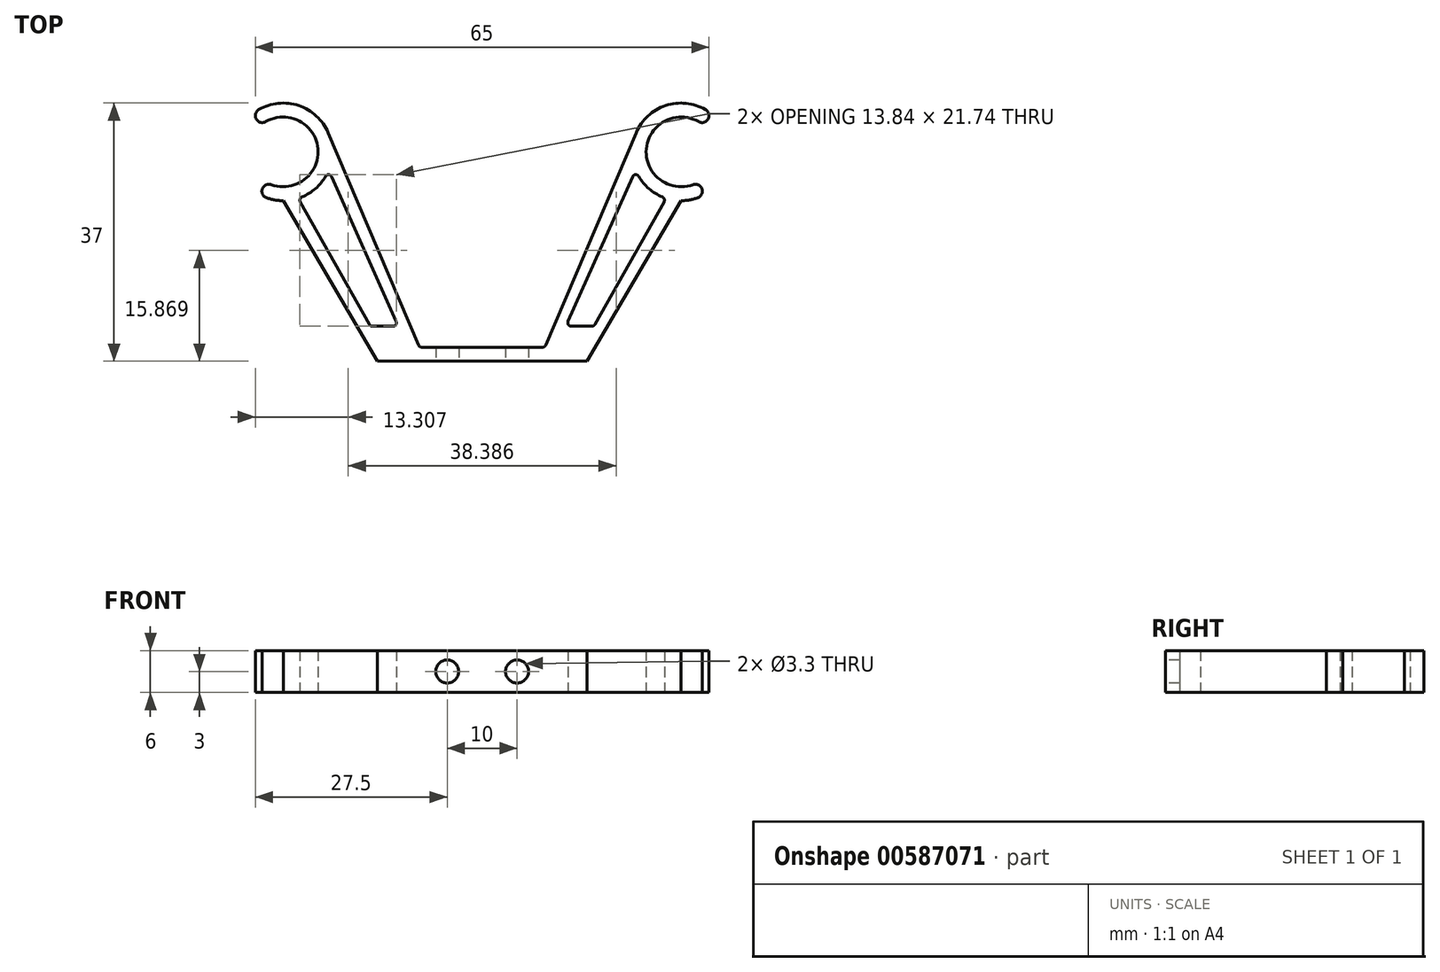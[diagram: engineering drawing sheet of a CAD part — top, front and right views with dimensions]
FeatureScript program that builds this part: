
annotation { "Feature Type Name" : "Feature", "Feature Type Description" : "" }
export const myFeature = defineFeature(function(context is Context, id is Id, definition is map)
    precondition{}
    {
        {
            var Q0;
            Q0=qCreatedBy(makeId("Top.planeOp"),FACE);
            var sketch = newSketch(context, id + "F0", { "sketchPlane" : qUnion([Q0])});
            skLineSegment(sketch, "E0", {"start": v(-28.5, 0) * mm, "end": v(28.5, 0) * mm, "construction": true});
            skArc(sketch, "E1", {"start": v(-31, 4.33) * mm, "mid": v(-23.52, 0.44) * mm, "end": v(-30.21, -4.7) * mm});
            skLineSegment(sketch, "E2", {"start": v(0, 15.66) * mm, "end": v(0, -18.65) * mm, "construction": true});
            skLineSegment(sketch, "E3", {"start": v(-31, 4.33) * mm, "end": v(-28.5, 0) * mm, "construction": true});
            skLineSegment(sketch, "E4", {"start": v(-30.21, -4.7) * mm, "end": v(-28.5, 0) * mm, "construction": true});
            skLineSegment(sketch, "E5", {"start": v(-15, -30) * mm, "end": v(0, -30) * mm});
            skArc(sketch, "E6.0", {"start": v(-32, 6.06) * mm, "mid": v(-26.28, 6.64) * mm, "end": v(-22.06, 2.74) * mm});
            skArc(sketch, "E7", {"start": v(-32, 6.06) * mm, "mid": v(-32.37, 4.7) * mm, "end": v(-31, 4.33) * mm});
            skLineSegment(sketch, "E8", {"start": v(-31, 4.33) * mm, "end": v(-32, 6.06) * mm, "construction": true});
            skLineSegment(sketch, "E9", {"start": v(-30.21, -4.7) * mm, "end": v(-30.9, -6.58) * mm, "construction": true});
            skArc(sketch, "E10", {"start": v(-30.21, -4.7) * mm, "mid": v(-31.5, -5.3) * mm, "end": v(-30.9, -6.58) * mm});
            skLineSegment(sketch, "E11", {"start": v(-15, -30) * mm, "end": v(-28.5, -7) * mm});
            skLineSegment(sketch, "E12", {"start": v(0, -28) * mm, "end": v(-8.67, -28) * mm});
            skLineSegment(sketch, "E13", {"start": v(-9.13, -27.7) * mm, "end": v(-22.06, 2.74) * mm});
            skLineSegment(sketch, "E14", {"start": v(-28.5, 0) * mm, "end": v(-28.5, -18.9) * mm, "construction": true});
            skLineSegment(sketch, "E15", {"start": v(-26.05, -7.17) * mm, "end": v(-16.14, -24.75) * mm});
            skLineSegment(sketch, "E16", {"start": v(-15.7, -25) * mm, "end": v(-12.77, -25) * mm});
            skLineSegment(sketch, "E17", {"start": v(-12.31, -24.3) * mm, "end": v(-21.55, -3.56) * mm});
            skArc(sketch, "E18.trimOffspring", {"start": v(-28.5, -7) * mm, "mid": v(-29.72, -6.9) * mm, "end": v(-30.9, -6.58) * mm});
            skArc(sketch, "E19.trimOffspring", {"start": v(-22.44, -3.5) * mm, "mid": v(-23.88, -5.26) * mm, "end": v(-25.8, -6.46) * mm});
            skLineSegment(sketch, "E20.MirrorCS", {"start": v(31, 4.33) * mm, "end": v(32, 6.06) * mm, "construction": true});
            skLineSegment(sketch, "E21.MirrorCS", {"start": v(30.21, -4.7) * mm, "end": v(30.9, -6.58) * mm, "construction": true});
            skLineSegment(sketch, "E22.MirrorCS", {"start": v(31, 4.33) * mm, "end": v(28.5, 0) * mm, "construction": true});
            skLineSegment(sketch, "E23.MirrorCS", {"start": v(30.21, -4.7) * mm, "end": v(28.5, 0) * mm, "construction": true});
            skLineSegment(sketch, "E24.MirrorCS", {"start": v(15, -30) * mm, "end": v(0, -30) * mm});
            skArc(sketch, "E25.MirrorCS", {"start": v(32, 6.06) * mm, "mid": v(26.28, 6.64) * mm, "end": v(22.06, 2.74) * mm});
            skArc(sketch, "E26.MirrorCS", {"start": v(32, 6.06) * mm, "mid": v(32.37, 4.7) * mm, "end": v(31, 4.33) * mm});
            skArc(sketch, "E27.MirrorCS", {"start": v(30.21, -4.7) * mm, "mid": v(31.5, -5.3) * mm, "end": v(30.9, -6.58) * mm});
            skLineSegment(sketch, "E28.MirrorCS", {"start": v(15, -30) * mm, "end": v(28.5, -7) * mm});
            skLineSegment(sketch, "E29.MirrorCS", {"start": v(0, -28) * mm, "end": v(8.67, -28) * mm});
            skArc(sketch, "E30.MirrorCS", {"start": v(22.44, -3.5) * mm, "mid": v(23.88, -5.26) * mm, "end": v(25.8, -6.46) * mm});
            skArc(sketch, "E31.MirrorCS", {"start": v(31, 4.33) * mm, "mid": v(23.52, 0.44) * mm, "end": v(30.21, -4.7) * mm});
            skLineSegment(sketch, "E32.MirrorCS", {"start": v(26.05, -7.17) * mm, "end": v(16.14, -24.75) * mm});
            skArc(sketch, "E33.MirrorCS", {"start": v(28.5, -7) * mm, "mid": v(29.72, -6.9) * mm, "end": v(30.9, -6.58) * mm});
            skLineSegment(sketch, "E34.MirrorCS", {"start": v(9.13, -27.7) * mm, "end": v(22.06, 2.74) * mm});
            skLineSegment(sketch, "E35.MirrorCS", {"start": v(28.5, 0) * mm, "end": v(28.5, -18.9) * mm, "construction": true});
            skLineSegment(sketch, "E36.MirrorCS", {"start": v(12.31, -24.3) * mm, "end": v(21.55, -3.56) * mm});
            skLineSegment(sketch, "E37.MirrorCS", {"start": v(15.7, -25) * mm, "end": v(12.77, -25) * mm});
            skLineSegment(sketch, "E38.MirrorCS", {"start": v(28.5, 0) * mm, "end": v(-28.5, 0) * mm, "construction": true});
            skPoint(sketch, "E39.visualSharp", {"position": v(-12, -25) * mm});
            skArc(sketch, "E39.filletArc", {"start": v(-12.77, -25) * mm, "mid": v(-12.35, -24.77) * mm, "end": v(-12.31, -24.3) * mm});
            skPoint(sketch, "E40.visualSharp", {"position": v(12, -25) * mm});
            skArc(sketch, "E40.filletArc", {"start": v(12.31, -24.3) * mm, "mid": v(12.35, -24.77) * mm, "end": v(12.77, -25) * mm});
            skPoint(sketch, "E41.visualSharp", {"position": v(9, -28) * mm});
            skArc(sketch, "E41.filletArc", {"start": v(8.67, -28) * mm, "mid": v(8.95, -27.92) * mm, "end": v(9.13, -27.7) * mm});
            skPoint(sketch, "E42.visualSharp", {"position": v(-9, -28) * mm});
            skArc(sketch, "E42.filletArc", {"start": v(-9.13, -27.7) * mm, "mid": v(-8.95, -27.92) * mm, "end": v(-8.67, -28) * mm});
            skPoint(sketch, "E43.visualSharp", {"position": v(16, -25) * mm});
            skArc(sketch, "E43.filletArc", {"start": v(15.7, -25) * mm, "mid": v(15.96, -24.93) * mm, "end": v(16.14, -24.75) * mm});
            skPoint(sketch, "E44.visualSharp", {"position": v(-16, -25) * mm});
            skArc(sketch, "E44.filletArc", {"start": v(-16.14, -24.75) * mm, "mid": v(-15.96, -24.93) * mm, "end": v(-15.7, -25) * mm});
            skPoint(sketch, "E45.visualSharp", {"position": v(-22, -2.58) * mm});
            skArc(sketch, "E45.filletArc", {"start": v(-21.55, -3.56) * mm, "mid": v(-21.98, -3.26) * mm, "end": v(-22.44, -3.5) * mm});
            skPoint(sketch, "E46.visualSharp", {"position": v(-26.34, -6.66) * mm});
            skArc(sketch, "E46.filletArc", {"start": v(-25.8, -6.46) * mm, "mid": v(-26.09, -6.76) * mm, "end": v(-26.05, -7.17) * mm});
            skPoint(sketch, "E47.visualSharp", {"position": v(22, -2.58) * mm});
            skArc(sketch, "E47.filletArc", {"start": v(22.44, -3.5) * mm, "mid": v(21.98, -3.26) * mm, "end": v(21.55, -3.56) * mm});
            skPoint(sketch, "E48.visualSharp", {"position": v(26.34, -6.66) * mm});
            skArc(sketch, "E48.filletArc", {"start": v(26.05, -7.17) * mm, "mid": v(26.09, -6.76) * mm, "end": v(25.8, -6.46) * mm});
            skSolve(sketch);
        }
        {
            var Q0;
            Q0 = qSketchRegion(id + "F0", true);
            extrude(context, id + "F1", {"entities" : qUnion([Q0]), "depth" : 6 * mm, "offsetDistance" : 25 * mm});
        }
        {
            var Q0;
            Q0=makeQuery(id+"F1.opExtrude","SWEPT_FACE",FACE,{"disambiguationData":[OSD([sQuery(id+"F0.wireOp",EDGE,"E5"),sQuery(id+"F0.wireOp",EDGE,"E24.MirrorCS")])]});
            var sketch = newSketch(context, id + "F2", { "sketchPlane" : qUnion([Q0])});
            skCircle(sketch, "E49", {"center": v(-5, 3) * mm, "radius": 1.65 * mm});
            skLineSegment(sketch, "E50", {"start": v(0, -2.58) * mm, "end": v(0, 9.22) * mm, "construction": true});
            skCircle(sketch, "E51.MirrorC", {"center": v(5, 3) * mm, "radius": 1.65 * mm});
            skSolve(sketch);
        }
        {
            var Q0;
            Q0 = qSketchRegion(id + "F2", true);
            extrude(context, id + "F3", {"entities" : qUnion([Q0]), "operationType" : NewBodyOperationType.REMOVE, "oppositeDirection" : true, "depth" : 25 * mm, "offsetDistance" : 25 * mm});
        }
    });
